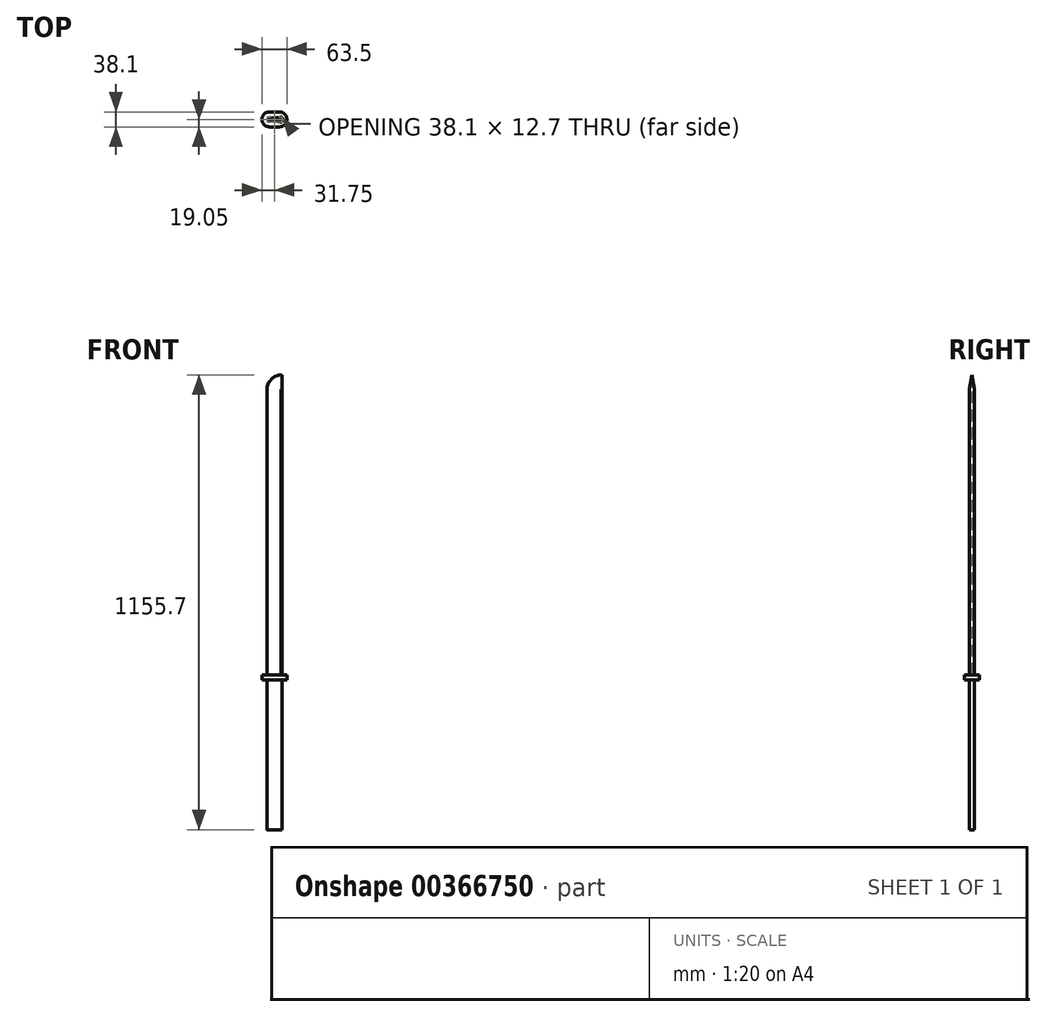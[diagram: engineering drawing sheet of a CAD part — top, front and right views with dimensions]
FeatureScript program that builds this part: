
annotation { "Feature Type Name" : "Feature", "Feature Type Description" : "" }
export const myFeature = defineFeature(function(context is Context, id is Id, definition is map)
    precondition{}
    {
        {
            var Q0;
            Q0=qCreatedBy(makeId("Front.planeOp"),FACE);
            var sketch = newSketch(context, id + "F0", { "sketchPlane" : qUnion([Q0])});
            skLineSegment(sketch, "E0", {"start": v(0, -107.67) * mm, "end": v(-19.05, -107.67) * mm});
            skLineSegment(sketch, "E1", {"start": v(-19.05, -107.67) * mm, "end": v(-19.05, 273.33) * mm});
            skLineSegment(sketch, "E2.MirrorCS", {"start": v(0, -107.67) * mm, "end": v(19.05, -107.67) * mm});
            skLineSegment(sketch, "E3.MirrorCS", {"start": v(19.05, -107.67) * mm, "end": v(19.05, 273.33) * mm});
            skLineSegment(sketch, "E4", {"start": v(-19.05, 273.33) * mm, "end": v(19.05, 273.33) * mm});
            skSolve(sketch);
        }
        {
            var Q0;
            Q0 = qSketchRegion(id + "F0", true);
            extrude(context, id + "F1", {"entities" : qUnion([Q0]), "depth" : 12.7 * mm});
        }
        {
            var Q0;
            Q0=makeQuery(id+"F1.opExtrude","SWEPT_FACE",FACE,{"disambiguationData":[OSD([sQuery(id+"F0.wireOp",EDGE,"E4")])]});
            var sketch = newSketch(context, id + "F2", { "sketchPlane" : qUnion([Q0])});
            skLineSegment(sketch, "E5", {"start": v(0, 0) * mm, "end": v(0, -12.7) * mm});
            skLineSegment(sketch, "E6", {"start": v(0, -12.7) * mm, "end": v(0, -6.35) * mm});
            skLineSegment(sketch, "E7.bottom", {"start": v(31.75, -25.4) * mm, "end": v(-31.75, -25.4) * mm});
            skLineSegment(sketch, "E7.top", {"start": v(31.75, 12.7) * mm, "end": v(-31.75, 12.7) * mm});
            skLineSegment(sketch, "E7.left", {"start": v(31.75, -25.4) * mm, "end": v(31.75, 12.7) * mm});
            skLineSegment(sketch, "E7.right", {"start": v(-31.75, -25.4) * mm, "end": v(-31.75, 12.7) * mm});
            skPoint(sketch, "E7.middle", {"position": v(0, -6.35) * mm});
            skSolve(sketch);
        }
        {
            var Q0;
            Q0 = qSketchRegion(id + "F2", true);
            extrude(context, id + "F3", {"entities" : qUnion([Q0]), "operationType" : NewBodyOperationType.ADD, "depth" : 12.7 * mm});
        }
        {
            var Q0;
            Q0=makeQuery(id+"F1.opExtrude","CAP_FACE",FACE,{"disambiguationData":[OSD([sQuery(id+"F0.wireOp",EDGE,"E0"),sQuery(id+"F0.wireOp",EDGE,"E1"),sQuery(id+"F0.wireOp",EDGE,"E2.MirrorCS"),sQuery(id+"F0.wireOp",EDGE,"E3.MirrorCS"),sQuery(id+"F0.wireOp",EDGE,"E4")])],"isStart":false});
            var sketch = newSketch(context, id + "F4", { "sketchPlane" : qUnion([Q0])});
            skLineSegment(sketch, "E8", {"start": v(-19.05, 273.33) * mm, "end": v(-19.05, 1048.03) * mm});
            skLineSegment(sketch, "E9.MirrorCS", {"start": v(19.05, 273.33) * mm, "end": v(19.05, 1048.03) * mm});
            skLineSegment(sketch, "E10", {"start": v(-19.05, 1048.03) * mm, "end": v(19.05, 1048.03) * mm});
            skSolve(sketch);
        }
        {
            var Q0;
            Q0=makeQuery(id+"F4.imprint","IMPRINT",FACE,{"disambiguationData":[TD([[makeQuery(id+"F4.imprint","IMPRINT",EDGE,{"derivedFrom":sQuery(id+"F4.wireOp",EDGE,"E8")}),-1.0]])]});
            extrude(context, id + "F5", {"entities" : qUnion([Q0]), "operationType" : NewBodyOperationType.ADD, "depth" : -12.7 * mm});
        }
        {
            var Q0;
            Q0=makeQuery(id+"F5.opExtrude","SWEPT_EDGE",EDGE,{"disambiguationData":[OSD([sQuery(id+"F4.wireOp",EDGE,"E8"),sQuery(id+"F4.wireOp",EDGE,"E10")])]});
            fillet(context, id + "F6", {"entities" : qUnion([Q0]), "radius" : 38.1 * mm, "tangentPropagation" : true, "rho" : 0, "crossSection" : FilletCrossSection.CONIC, "allowEdgeOverflow" : false});
        }
        {
            var Q0;
            Q0=makeQuery(id+"F1.opExtrude","CAP_EDGE",EDGE,{"disambiguationData":[OSD([sQuery(id+"F0.wireOp",EDGE,"E1")])],"isStart":false});
            var Q1;
            Q1=makeQuery(id+"F1.opExtrude","CAP_EDGE",EDGE,{"disambiguationData":[OSD([sQuery(id+"F0.wireOp",EDGE,"E1")])],"isStart":true});
            var Q2;
            Q2=makeQuery(id+"F1.opExtrude","CAP_EDGE",EDGE,{"disambiguationData":[OSD([sQuery(id+"F0.wireOp",EDGE,"E3.MirrorCS")])],"isStart":true});
            var Q3;
            Q3=makeQuery(id+"F1.opExtrude","CAP_EDGE",EDGE,{"disambiguationData":[OSD([sQuery(id+"F0.wireOp",EDGE,"E3.MirrorCS")])],"isStart":false});
            fillet(context, id + "F7", {"entities" : qUnion([Q0, Q1, Q2, Q3]), "radius" : 6.35 * mm, "tangentPropagation" : true, "allowEdgeOverflow" : false});
        }
        {
            var Q0;
            Q0=makeQuery(id+"F3.opExtrude","SWEPT_EDGE",EDGE,{"disambiguationData":[OSD([sQuery(id+"F2.wireOp",EDGE,"E7.top"),sQuery(id+"F2.wireOp",EDGE,"E7.left")])]});
            var Q1;
            Q1=makeQuery(id+"F3.opExtrude","SWEPT_EDGE",EDGE,{"disambiguationData":[OSD([sQuery(id+"F2.wireOp",EDGE,"E7.bottom"),sQuery(id+"F2.wireOp",EDGE,"E7.left")])]});
            var Q2;
            Q2=makeQuery(id+"F3.opExtrude","SWEPT_EDGE",EDGE,{"disambiguationData":[OSD([sQuery(id+"F2.wireOp",EDGE,"E7.top"),sQuery(id+"F2.wireOp",EDGE,"E7.right")])]});
            var Q3;
            Q3=makeQuery(id+"F3.opExtrude","SWEPT_EDGE",EDGE,{"disambiguationData":[OSD([sQuery(id+"F2.wireOp",EDGE,"E7.bottom"),sQuery(id+"F2.wireOp",EDGE,"E7.right")])]});
            fillet(context, id + "F8", {"entities" : qUnion([Q0, Q1, Q2, Q3]), "radius" : 19.05 * mm, "tangentPropagation" : true, "allowEdgeOverflow" : false});
        }
        {
            var Q0;
            Q0=makeQuery(id+"F5.opExtrude","CAP_EDGE",EDGE,{"disambiguationData":[OSD([sQuery(id+"F4.wireOp",EDGE,"E8")])],"isStart":true});
            var Q1;
            Q1=makeQuery(id+"F5.opExtrude","CAP_EDGE",EDGE,{"disambiguationData":[OSD([sQuery(id+"F4.wireOp",EDGE,"E8")])],"isStart":false});
            chamfer(context, id + "F9", {"entities" : qUnion([Q0, Q1]), "chamferType" : ChamferType.OFFSET_ANGLE, "width" : 6.35 * mm, "oppositeDirection" : false, "angle" : 80 * degree, "tangentPropagation" : true});
        }
    });
